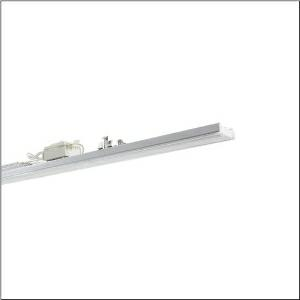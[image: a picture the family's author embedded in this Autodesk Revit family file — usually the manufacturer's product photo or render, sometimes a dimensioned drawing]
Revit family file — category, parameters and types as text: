
# Revit family: licross_r__11_recessed_ho_51te12mn4exm_0e74
name_source: partatom
category: Lighting Fixtures
units: mm (PartAtom-declared; Revit-internal decimal feet)

## family parameters
Cut with Voids When Loaded = No
Host = Face
Light Source = No
Part Type = Normal
Room Calculation Point = No
Round Connector Dimension = Use Diameter
Shared = No

## types (1)
- --- (1 x LED, 14100 lm, 74.5 W, 4000K)
    Apparent Load = 75 VA
    CIE Flux Codes = 66 91 98 100 100
    Color Rendering = 80
    Color Temperature = 4000K
    Default Elevation = 1800 mm
    Description = Licross® 11 Recessed HO, luminaire insert, of sheet steel, galvanised, coil coated, white, length: 1.500mm, width: 66mm, height: 67mm, LED rated luminous flux: 14.100lm, light colour: 840, control gear: ON/OFF Multilumen, with plug, 3-pole, with phase selection, mains connection: 220..240V, AC, 50/60Hz, rated input power: 75W, halogen-free wiring, primary optical cover: cover, of PMMA, light emission: direct distribution, primary light characteristic: symmetric, protection rating (complete): IP54, insulation class (complete): insulation class I (protective earthing), certification: CE, ENEC, VDE, UKCA, protection symbol: D if used in an environment with non-conductive dust loads with corresponding accessories, impact resistance: IK06, permissible ambient temperature for indoor applications: -35..+35°C, corresponds to IFS (International Featured Standards) requirements for safety and quality in the food industry, reducing of maximum allowable ambient temperature of 5°C with ceiling mounting, packaging unit: 1 piece
    Height = 58 mm
    Lamp = 1 x LED
    Lamp Light Flux = 14100 lm
    Lamp Power = 74.5 W
    Lamp count = 1
    Length = 1500 mm
    Luminous efficacy = 189 lm/W
    Manufacturer = Siteco
    ModVariant = No
    Model = 51TE12MN4EXM
    Mounting Place = Ceiling
    Mounting Type = Pendant
    Number of Poles = 1
    OnlyDefault = Yes
    Power Factor = 1
    Product Name = Licross® 11 Recessed HO
    Product group = luminaire insert
    ProductGroupID = 902
    Protection Class = Protection class I
    Protection Degree = IP 54
    RLX_Detail_Level = 1
    RLX_Emergency_Light_Flux = 0 lm
    RLX_Emergency_Type = 0
    RLX_Emergency_Type_DB = No
    RlxData = <blob elided: 22145 chars, md5=96e2dfbe>
    Socket = socket
    Standby Power = 0 W
    System Light Flux = 14100 lm
    System Power = 75 W
    Type Comments = factory setting: luminous flux: 100 % | (A | C | E) | 174 mA
    Type Image = l_1296930.jpg
    URL = http://relux.com
    VarID = @adj_085106
    Voltage = 0 V
    Weight = 0.00 kg
    Width = 66 mm

## geometry (parser evidence)
native form markers: Blend x4, Sweep x12
no freeform markers — native parametric forms only
